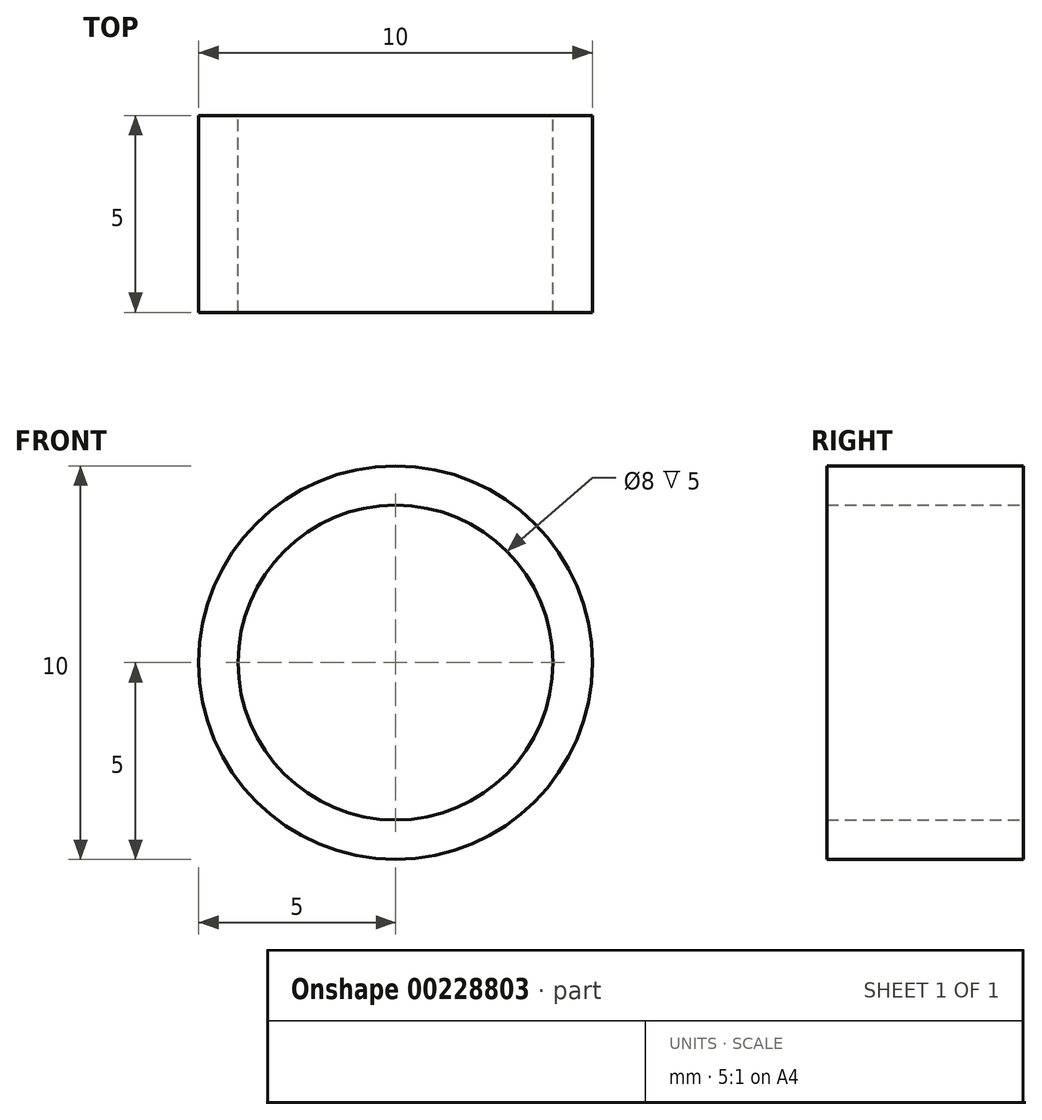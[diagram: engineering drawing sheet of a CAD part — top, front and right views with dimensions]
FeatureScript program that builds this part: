
annotation { "Feature Type Name" : "Feature", "Feature Type Description" : "" }
export const myFeature = defineFeature(function(context is Context, id is Id, definition is map)
    precondition{}
    {
        {
            var Q0;
            Q0=qCreatedBy(makeId("Front.planeOp"),FACE);
            var sketch = newSketch(context, id + "F0", { "sketchPlane" : qUnion([Q0])});
            skCircle(sketch, "E0", {"center": v(0, 0) * mm, "radius": 4 * mm});
            skCircle(sketch, "E1", {"center": v(0, 0) * mm, "radius": 5 * mm});
            skSolve(sketch);
        }
        {
            var Q0;
            Q0=makeQuery(id+"F0.imprint","IMPRINT",FACE,{"disambiguationData":[TD([[makeQuery(id+"F0.imprint","IMPRINT",EDGE,{"derivedFrom":sQuery(id+"F0.wireOp",EDGE,"E0")}),-1.0]])]});
            extrude(context, id + "F1", {"entities" : qUnion([Q0]), "endBound" : BoundingType.SYMMETRIC, "depth" : 5 * mm});
        }
    });
